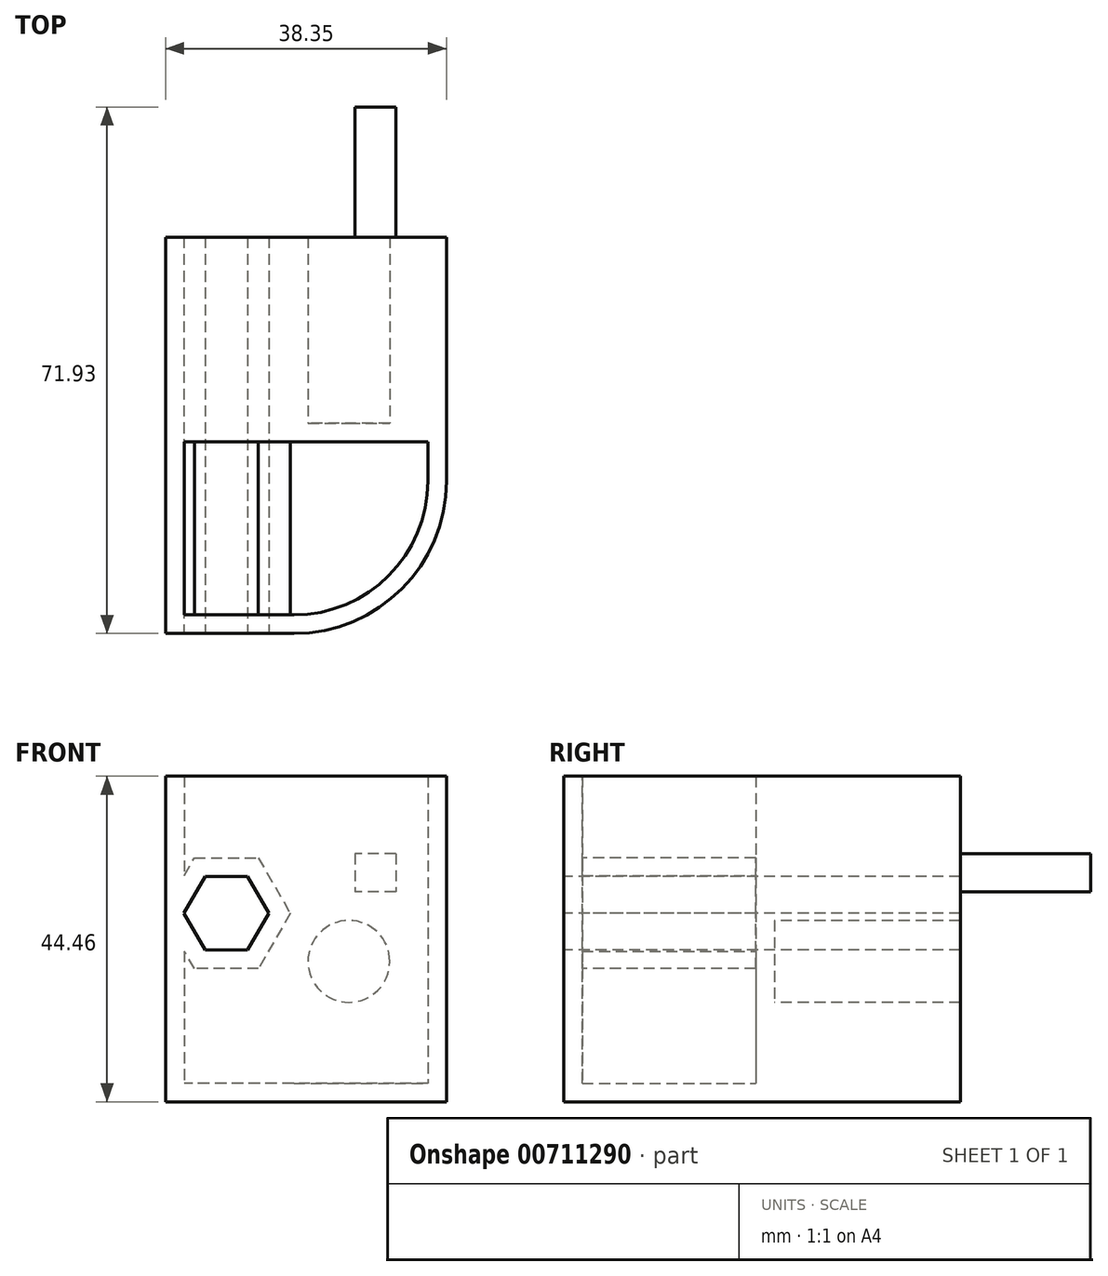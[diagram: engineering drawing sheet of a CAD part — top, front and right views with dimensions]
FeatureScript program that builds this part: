
annotation { "Feature Type Name" : "Feature", "Feature Type Description" : "" }
export const myFeature = defineFeature(function(context is Context, id is Id, definition is map)
    precondition{}
    {
        {
            var Q0;
            Q0=qCreatedBy(makeId("Right.planeOp"),FACE);
            var sketch = newSketch(context, id + "F0", { "sketchPlane" : qUnion([Q0])});
            skLineSegment(sketch, "E0.bottom", {"start": v(-59.9, 30.85) * mm, "end": v(-31.14, 30.85) * mm});
            skLineSegment(sketch, "E0.top", {"start": v(-59.9, 11.54) * mm, "end": v(-31.14, 11.54) * mm});
            skLineSegment(sketch, "E0.left", {"start": v(-59.9, 30.85) * mm, "end": v(-59.9, 11.54) * mm});
            skLineSegment(sketch, "E0.right", {"start": v(-31.14, 30.85) * mm, "end": v(-31.14, 11.54) * mm});
            skSolve(sketch);
        }
        {
            var Q0;
            Q0=makeQuery(id+"F0.imprint","IMPRINT",FACE,{"disambiguationData":[TD([[makeQuery(id+"F0.imprint","IMPRINT",EDGE,{"derivedFrom":sQuery(id+"F0.wireOp",EDGE,"E0.bottom")}),-1.0]])]});
            extrude(context, id + "F1", {"entities" : qUnion([Q0]), "depth" : 38.35 * mm, "offsetDistance" : 25.4 * mm});
        }
        {
            var Q0;
            Q0=makeQuery(id+"F1.opExtrude","SWEPT_FACE",FACE,{"disambiguationData":[OSD([sQuery(id+"F0.wireOp",EDGE,"E0.bottom")])]});
            extrude(context, id + "F2", {"entities" : qUnion([Q0]), "operationType" : NewBodyOperationType.ADD, "depth" : 25.15 * mm, "offsetDistance" : 25.4 * mm});
        }
        {
            var Q0;
            {var subQ0=sQuery(id+"F0.wireOp",EDGE,"E0.left");var subQ1=sQuery(id+"F0.wireOp",EDGE,"E0.bottom");Q0=makeQuery(id+"F2.boolean.opBoolean","MERGE",EDGE,{"derivedFrom":[makeQuery(id+"F1.opExtrude","CAP_EDGE",EDGE,{"disambiguationData":[OSD([subQ0])],"isStart":false}),makeQuery(id+"F2.opExtrude","SWEPT_EDGE",EDGE,{"disambiguationData":[OSD([subQ1,subQ0]),TDD([makeQuery(id+"F1.opExtrude","CAP_VERTEX",VERTEX,{"disambiguationData":[OSD([subQ1,subQ0])],"isStart":false})])]})]});}
            fillet(context, id + "F3", {"entities" : qUnion([Q0]), "radius" : 20.85 * mm, "tangentPropagation" : true, "allowEdgeOverflow" : false});
        }
        {
            var Q0;
            {var subQ0=sQuery(id+"F0.wireOp",EDGE,"E0.left");Q0=makeQuery(id+"F2.boolean.opBoolean","MERGE",FACE,{"derivedFrom":[makeQuery(id+"F1.opExtrude","SWEPT_FACE",FACE,{"disambiguationData":[OSD([subQ0])]}),makeQuery(id+"F2.opExtrude","SWEPT_FACE",FACE,{"disambiguationData":[OSD([sQuery(id+"F0.wireOp",EDGE,"E0.bottom"),subQ0])]})]});}
            var sketch = newSketch(context, id + "F4", { "sketchPlane" : qUnion([Q0])});
            skCircle(sketch, "E1.cCircle", {"center": v(8.3, 37.28) * mm, "radius": 5.03 * mm, "construction": true});
            skLineSegment(sketch, "E1.0", {"start": v(11.2, 32.26) * mm, "end": v(5.39, 32.26) * mm});
            skLineSegment(sketch, "E1.1", {"start": v(5.39, 32.26) * mm, "end": v(2.49, 37.28) * mm});
            skLineSegment(sketch, "E1.2", {"start": v(2.49, 37.28) * mm, "end": v(5.39, 42.31) * mm});
            skLineSegment(sketch, "E1.3", {"start": v(5.39, 42.31) * mm, "end": v(11.2, 42.31) * mm});
            skLineSegment(sketch, "E1.4", {"start": v(11.2, 42.31) * mm, "end": v(14.1, 37.28) * mm});
            skLineSegment(sketch, "E1.5", {"start": v(14.1, 37.28) * mm, "end": v(11.2, 32.26) * mm});
            skPoint(sketch, "E1.0.midPoint", {"position": v(8.3, 32.26) * mm});
            skSolve(sketch);
        }
        {
            var Q0;
            Q0=makeQuery(id+"F4.imprint","IMPRINT",FACE,{"disambiguationData":[TD([[makeQuery(id+"F4.imprint","IMPRINT",EDGE,{"derivedFrom":sQuery(id+"F4.wireOp",EDGE,"E1.0")}),-1.0]])]});
            extrude(context, id + "F5", {"entities" : qUnion([Q0]), "operationType" : NewBodyOperationType.REMOVE, "oppositeDirection" : true, "depth" : 29.97 * mm, "offsetDistance" : 25.4 * mm});
        }
        {
            var Q0;
            Q0=makeQuery(id+"F2.opExtrude","CAP_FACE",FACE,{"disambiguationData":[OSD([sQuery(id+"F0.wireOp",EDGE,"E0.bottom")])],"isStart":false});
            shell(context, id + "F6", {"entities" : qUnion([Q0]), "thickness" : 2.54 * mm});
        }
        {
            var Q0;
            {var subQ0=sQuery(id+"F0.wireOp",EDGE,"E0.right");Q0=makeQuery(id+"F2.boolean.opBoolean","MERGE",FACE,{"derivedFrom":[makeQuery(id+"F1.opExtrude","SWEPT_FACE",FACE,{"disambiguationData":[OSD([subQ0])]}),makeQuery(id+"F2.opExtrude","SWEPT_FACE",FACE,{"disambiguationData":[OSD([sQuery(id+"F0.wireOp",EDGE,"E0.bottom"),subQ0])]})]});}
            var sketch = newSketch(context, id + "F7", { "sketchPlane" : qUnion([Q0])});
            skCircle(sketch, "E2", {"center": v(-25.02, 30.72) * mm, "radius": 5.59 * mm});
            skSolve(sketch);
        }
        {
            var Q0;
            Q0=makeQuery(id+"F7.imprint","IMPRINT",FACE,{"disambiguationData":[TD([[makeQuery(id+"F7.imprint","IMPRINT",EDGE,{"derivedFrom":sQuery(id+"F7.wireOp",EDGE,"E2")}),1.0]])]});
            var sketch = newSketch(context, id + "F8", { "sketchPlane" : qUnion([Q0])});
            skLineSegment(sketch, "E3.bottom", {"start": v(-25.86, 40.22) * mm, "end": v(-31.42, 40.22) * mm});
            skLineSegment(sketch, "E3.top", {"start": v(-25.86, 45.45) * mm, "end": v(-31.42, 45.45) * mm});
            skLineSegment(sketch, "E3.left", {"start": v(-25.86, 40.22) * mm, "end": v(-25.86, 45.45) * mm});
            skLineSegment(sketch, "E3.right", {"start": v(-31.42, 40.22) * mm, "end": v(-31.42, 45.45) * mm});
            skSolve(sketch);
        }
        {
            var Q0;
            Q0=makeQuery(id+"F8.imprint","IMPRINT",FACE,{"disambiguationData":[TD([[makeQuery(id+"F8.imprint","IMPRINT",EDGE,{"derivedFrom":sQuery(id+"F8.wireOp",EDGE,"E3.bottom")}),-1.0]])]});
            extrude(context, id + "F9", {"entities" : qUnion([Q0]), "operationType" : NewBodyOperationType.ADD, "depth" : 17.78 * mm, "offsetDistance" : 25.4 * mm});
        }
        {
            var Q0;
            Q0=makeQuery(id+"F9.opExtrude","CAP_FACE",FACE,{"disambiguationData":[OSD([sQuery(id+"F8.wireOp",EDGE,"E3.bottom"),sQuery(id+"F8.wireOp",EDGE,"E3.top"),sQuery(id+"F8.wireOp",EDGE,"E3.left"),sQuery(id+"F8.wireOp",EDGE,"E3.right")])],"isStart":false});
            var Q1;
            Q1=makeQuery(id+"F7.imprint","IMPRINT",FACE,{"disambiguationData":[TD([[makeQuery(id+"F7.imprint","IMPRINT",EDGE,{"derivedFrom":sQuery(id+"F7.wireOp",EDGE,"E2")}),-1.0]])]});
            extrude(context, id + "F10", {"entities" : qUnion([Q0, Q1]), "operationType" : NewBodyOperationType.ADD, "depth" : 25.4 * mm, "offsetDistance" : 25.4 * mm});
        }
    });
